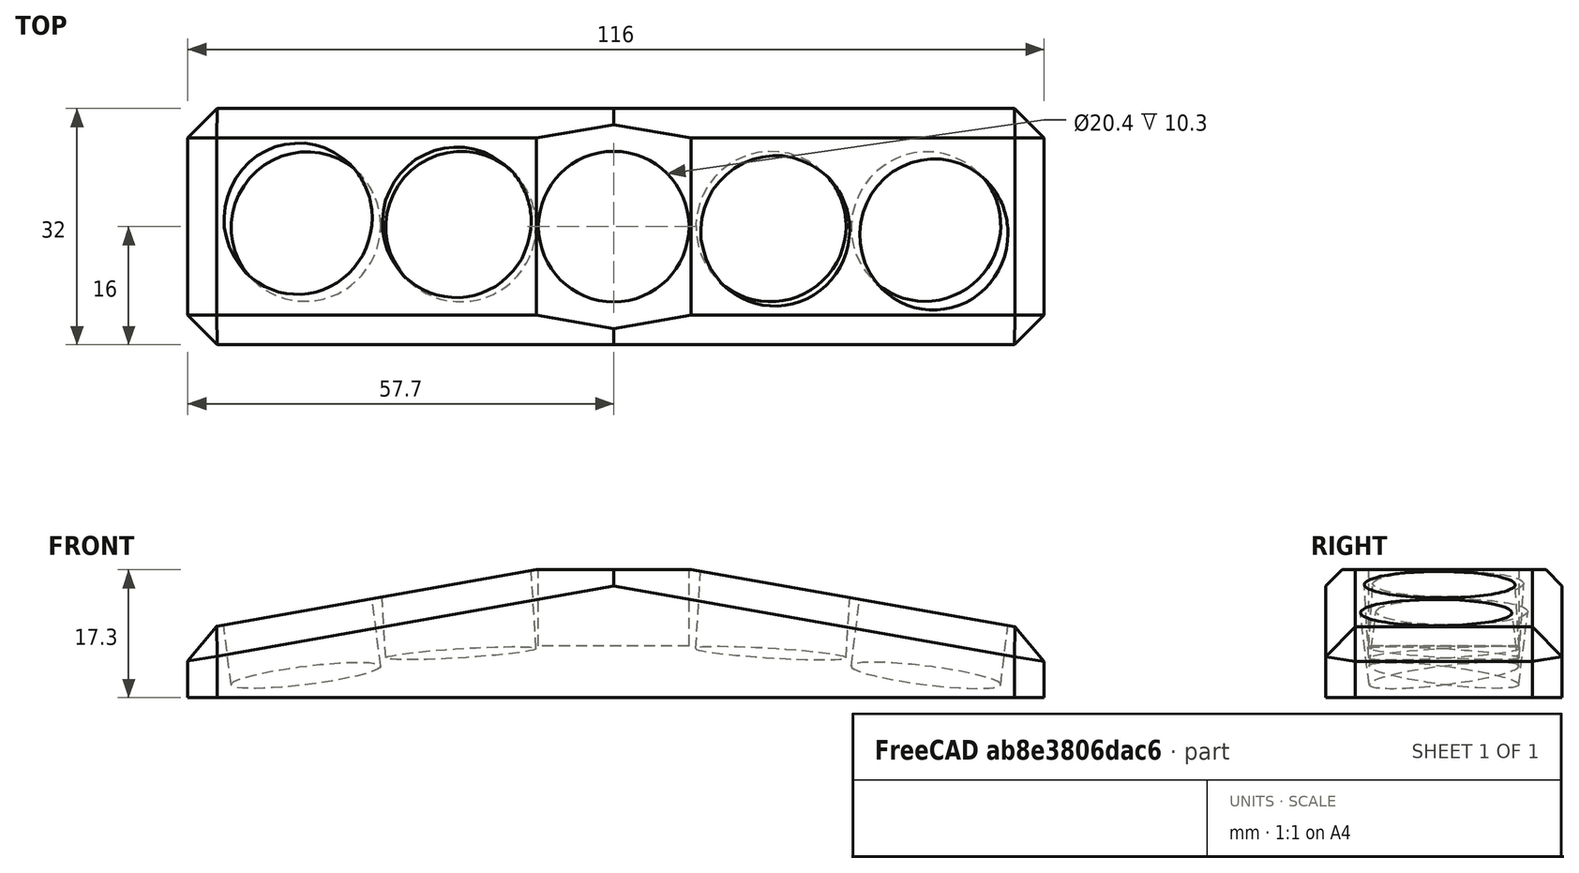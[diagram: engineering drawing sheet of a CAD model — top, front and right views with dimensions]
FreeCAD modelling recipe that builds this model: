
FCSTD DOCUMENT  (FreeCAD 0.16R)
Label: toothbrush-stand-v2-1
License: All rights reserved
LicenseURL: http://en.wikipedia.org/wiki/All_rights_reserved
objects: Part::Cut×8, Part::Cylinder×5, Part::Box×4, Part::Chamfer×1
note: 18 computed .brp shape members not serialized (recipe doc carries the construction recipe); baked Part::Feature solids carry a one-line shape summary decoded from their .brp

FEATURE [Part::Box] Box  label="Cube"
  Height = 20
  Length = 116
  Placement = pos=(-16,-16,-7) rot=(0,0,1;0rad)
  Width = 32
FEATURE [Part::Box] Box001  label="Cube001"
  Height = 14
  Length = 116
  Placement = pos=(-30,-16,-0.5) rot=(0,-1,0;0.174533rad)
  Width = 32
FEATURE [Part::Box] Box002  label="Cube002"
  Height = 14
  Length = 116
  Placement = pos=(0,-16,19.5) rot=(0,1,0;0.174533rad)
  Width = 32
FEATURE [Part::Cut] Cut005
  Base = -> Box
  Tool = -> Box001
FEATURE [Part::Cut] Cut006
  Base = -> Cut005
  Tool = -> Box002
FEATURE [Part::Chamfer] Chamfer
  Base = -> Cut006
  Edges = 10 edges r=4: [Edge1,Edge2,Edge3,Edge5,Edge6,Edge7,Edge9,Edge11,Edge12,Edge15]
FEATURE [Part::Cylinder] Cylinder010
  Angle = 360
  Height = 20
  Placement = pos=(0,0,-4) rot=(-0.707107,-0.707107,0;0.174533rad)
  Radius = 10.2
FEATURE [Part::Cylinder] Cylinder011
  Angle = 360
  Height = 20
  Placement = pos=(21,0,-1) rot=(-0.707107,-0.707107,0;0.087266rad)
  Radius = 10.2
FEATURE [Part::Cylinder] Cylinder012
  Angle = 360
  Height = 20
  Placement = pos=(41.7,0,0) rot=(0,0,1;0rad)
  Radius = 10.2
FEATURE [Part::Cylinder] Cylinder013
  Angle = 360
  Height = 20
  Placement = pos=(63,0,-1) rot=(0.707107,0.707107,0;0.087266rad)
  Radius = 10.2
FEATURE [Part::Cylinder] Cylinder014
  Angle = 360
  Height = 20
  Placement = pos=(84,0,-4) rot=(0.707107,0.707107,0;0.174533rad)
  Radius = 10.2
FEATURE [Part::Cut] Cut
  Base = -> Chamfer
  Tool = -> Cylinder010
FEATURE [Part::Cut] Cut007
  Base = -> Cut
  Tool = -> Cylinder011
FEATURE [Part::Cut] Cut008
  Base = -> Cut007
  Tool = -> Cylinder012
FEATURE [Part::Cut] Cut009
  Base = -> Cut008
  Tool = -> Cylinder013
FEATURE [Part::Cut] Cut010
  Base = -> Cut009
  Tool = -> Cylinder014
FEATURE [Part::Box] Box003  label="Cube003"
  Height = 10
  Length = 40
  Placement = pos=(20,-20,10.3) rot=(0,0,1;0rad)
  Width = 40
FEATURE [Part::Cut] Cut011
  Base = -> Cut010
  Tool = -> Box003
